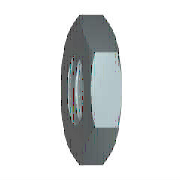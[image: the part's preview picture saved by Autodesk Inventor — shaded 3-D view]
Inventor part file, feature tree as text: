
AUTODESK INVENTOR PART (.ipt)
format: ipt  version: 2018 (Build 220112000, 112)  size: 165,376 bytes
history: native  units: mm (DEFAULTED — no unit token found)
features: sketch x3, other x2, extrude x1, hole x1, plane x1
ambient origin geometry x7: Origin, YZ Plane, XZ Plane, X Axis, Y Axis, Z Axis, Center Point
bodies: Solid1 (feature_tree)
feature tree (8):
  extrude  "Corpo"  Depth=15.011107mm
  other  "Smusso1"
  hole  "Filettatura"  [1 undecoded]
  other  "Work Axis1"
  plane  "Work Plane1"
  sketch  "Schizzo1"
  sketch  "Schizzo2"
  sketch  "Schizzo3"
note: 1 required parameter value undecoded (feature->parameter linkage not recoverable at this tier; creation-order binding heuristic only, values carry confidence <= 0.55)
